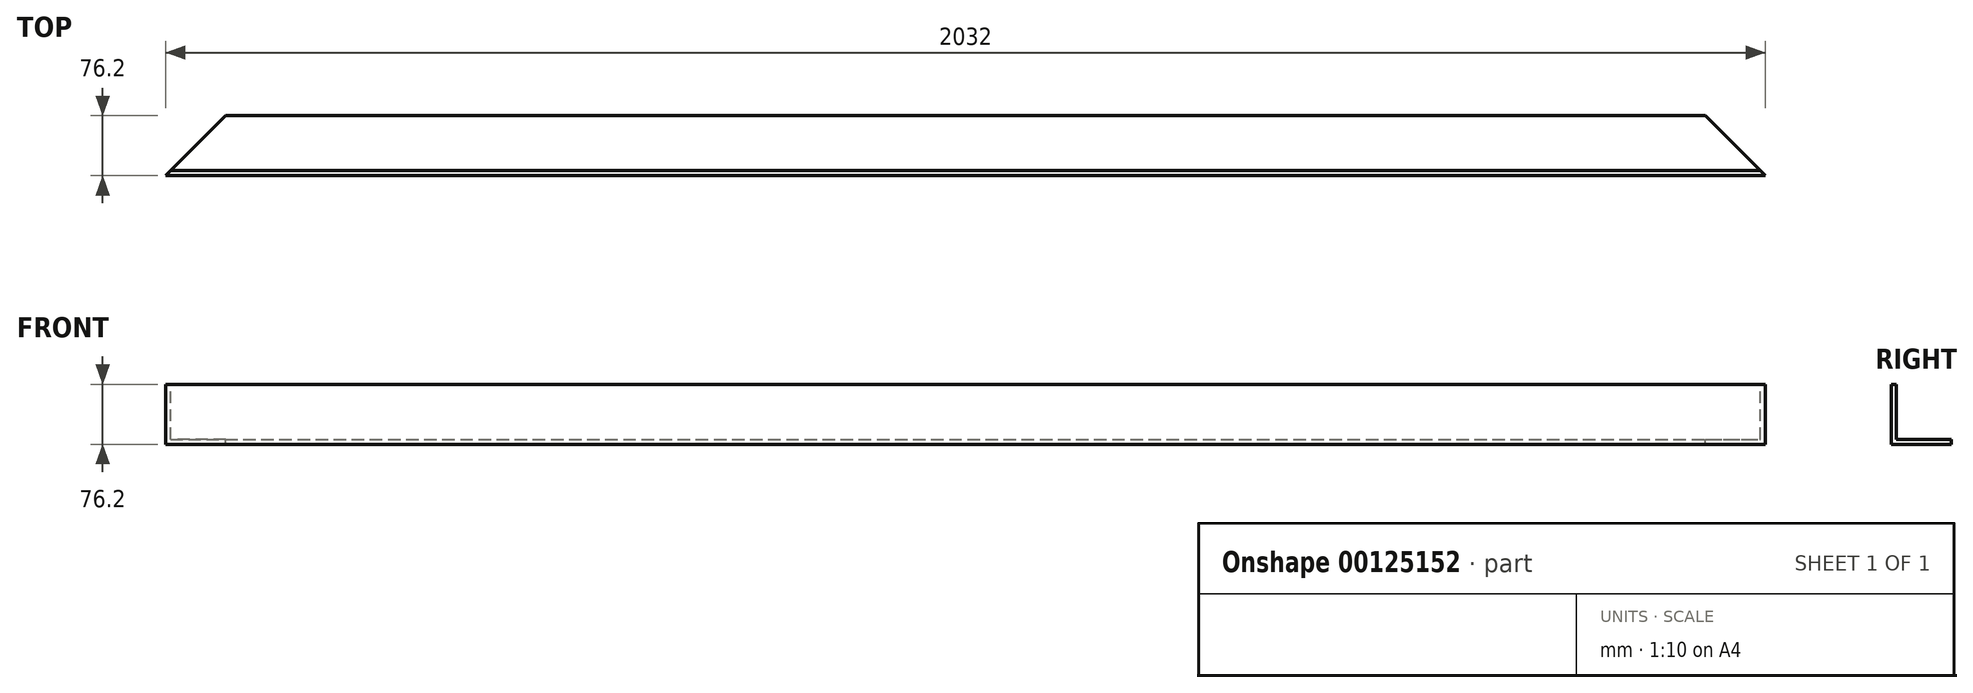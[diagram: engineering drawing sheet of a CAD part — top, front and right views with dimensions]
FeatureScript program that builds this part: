
annotation { "Feature Type Name" : "Feature", "Feature Type Description" : "" }
export const myFeature = defineFeature(function(context is Context, id is Id, definition is map)
    precondition{}
    {
        {
            var Q0;
            Q0=qCreatedBy(makeId("Right.planeOp"),FACE);
            var sketch = newSketch(context, id + "F0", { "sketchPlane" : qUnion([Q0])});
            skLineSegment(sketch, "E0", {"start": v(0, 76.2) * mm, "end": v(0, 0) * mm});
            skLineSegment(sketch, "E1", {"start": v(0, 0) * mm, "end": v(76.2, 0) * mm});
            skLineSegment(sketch, "E2.0", {"start": v(6.35, 6.35) * mm, "end": v(76.2, 6.35) * mm});
            skLineSegment(sketch, "E2.1", {"start": v(6.35, 76.2) * mm, "end": v(6.35, 6.35) * mm});
            skLineSegment(sketch, "E3", {"start": v(0, 76.2) * mm, "end": v(6.35, 76.2) * mm});
            skLineSegment(sketch, "E4", {"start": v(76.2, 6.35) * mm, "end": v(76.2, 0) * mm});
            skSolve(sketch);
        }
        {
            var Q0;
            Q0=qSketchRegion(id+"F0",true);
            extrude(context, id + "F1", {"entities" : qUnion([Q0]), "oppositeDirection" : true, "depth" : 2032 * mm});
        }
        {
            var Q0;
            Q0=makeQuery(id+"F1.opExtrude","SWEPT_FACE",FACE,{"disambiguationData":[OSD([sQuery(id+"F0.wireOp",EDGE,"E3")])]});
            var sketch = newSketch(context, id + "F2", { "sketchPlane" : qUnion([Q0])});
            skLineSegment(sketch, "E5", {"start": v(0, 76.2) * mm, "end": v(0, 0) * mm});
            skLineSegment(sketch, "E6", {"start": v(0, 0) * mm, "end": v(-76.2, 76.2) * mm});
            skLineSegment(sketch, "E7.trimOffspring", {"start": v(-76.2, 76.2) * mm, "end": v(0, 76.2) * mm});
            skLineSegment(sketch, "E8", {"start": v(-2032, 0) * mm, "end": v(-1955.8, 76.2) * mm});
            skLineSegment(sketch, "E9", {"start": v(-2032, 0) * mm, "end": v(-2032, 76.2) * mm});
            skLineSegment(sketch, "E10", {"start": v(-2032, 76.2) * mm, "end": v(-1955.8, 76.2) * mm});
            skSolve(sketch);
        }
        {
            var Q0;
            Q0=qSketchRegion(id+"F2",true);
            extrude(context, id + "F3", {"entities" : qUnion([Q0]), "operationType" : NewBodyOperationType.REMOVE, "oppositeDirection" : true, "depth" : 76.2 * mm});
        }
    });
